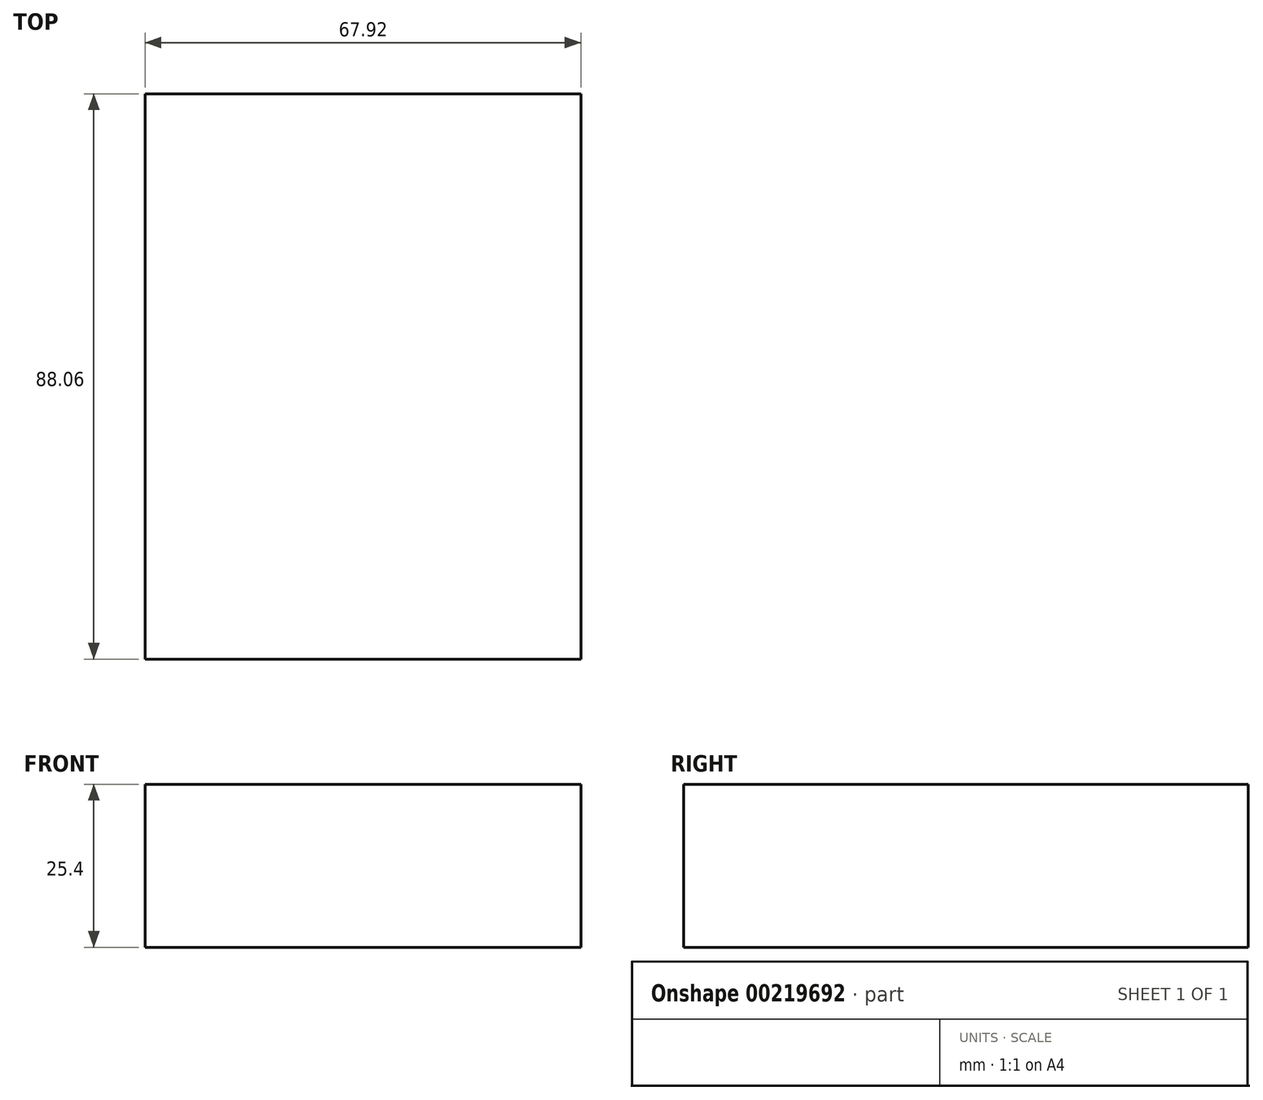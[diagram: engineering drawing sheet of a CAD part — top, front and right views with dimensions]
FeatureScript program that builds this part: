
annotation { "Feature Type Name" : "Feature", "Feature Type Description" : "" }
export const myFeature = defineFeature(function(context is Context, id is Id, definition is map)
    precondition{}
    {
        {
            var Q0;
            Q0=qCreatedBy(makeId("Top.planeOp"),FACE);
            var sketch = newSketch(context, id + "F0", { "sketchPlane" : qUnion([Q0])});
            skLineSegment(sketch, "E0.bottom", {"start": v(33.96, 44.03) * mm, "end": v(-33.96, 44.03) * mm});
            skLineSegment(sketch, "E0.top", {"start": v(33.96, -44.03) * mm, "end": v(-33.96, -44.03) * mm});
            skLineSegment(sketch, "E0.left", {"start": v(33.96, 44.03) * mm, "end": v(33.96, -44.03) * mm});
            skLineSegment(sketch, "E0.right", {"start": v(-33.96, 44.03) * mm, "end": v(-33.96, -44.03) * mm});
            skPoint(sketch, "E0.middle", {"position": v(0, 0) * mm});
            skSolve(sketch);
        }
        {
            var Q0;
            Q0=makeQuery(id+"F0.imprint","IMPRINT",FACE,{"disambiguationData":[TD([[makeQuery(id+"F0.imprint","IMPRINT",EDGE,{"derivedFrom":sQuery(id+"F0.wireOp",EDGE,"E0.bottom")}),1.0]])]});
            extrude(context, id + "F1", {"entities" : qUnion([Q0]), "depth" : 25.4 * mm});
        }
        {
            var Q0;
            Q0 = qSketchRegion(id + "F0", true);
            extrude(context, id + "F2", {"entities" : qUnion([Q0]), "depth" : 25.4 * mm});
        }
        {
            var Q0;
            Q0=makeQuery(id+"F0.imprint","IMPRINT",FACE,{"disambiguationData":[TD([[makeQuery(id+"F0.imprint","IMPRINT",EDGE,{"derivedFrom":sQuery(id+"F0.wireOp",EDGE,"E0.bottom")}),1.0]])]});
            extrude(context, id + "F3", {"entities" : qUnion([Q0]), "depth" : 25.4 * mm});
        }
    });
